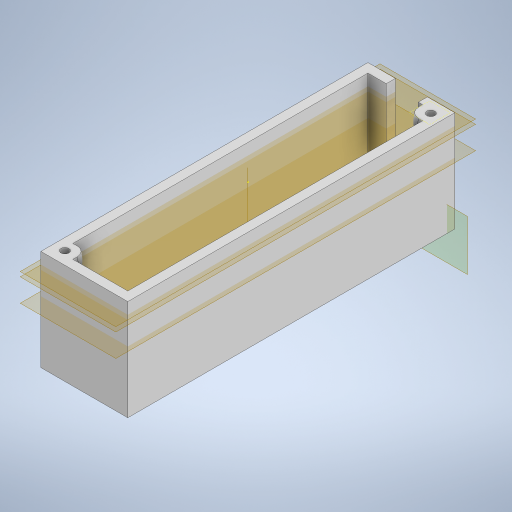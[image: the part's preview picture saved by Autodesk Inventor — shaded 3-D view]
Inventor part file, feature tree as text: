
AUTODESK INVENTOR PART (.ipt)
format: ipt  version: 2024 (Build 280153020, 153B)  size: 375,808 bytes
history: native  units: mm
features: sketch x9, extrude x6, plane x4, hole x1, loft x1, fillet x1, pattern_circular x1, projected_geometry x1, other x1
ambient origin geometry x8: Origin, YZ Plane, XZ Plane, XY Plane, X Axis, Y Axis, Z Axis, Center Point
bodies: Solid1 (feature_tree)
feature tree (25):
  sketch  "Sketch1"  dims[d0=30.0mm d1=135.0mm]
  extrude  "Extrusion1"  Depth=135.0mm
  extrude  "Extrusion2"  Depth=44.0mm TaperAngle=0.0deg
  hole  "Hole1"  [1 undecoded]
  plane  "Work Plane1"
  extrude  "Extrusion3"  Depth=14.0mm
  sketch  "Sketch4"  dims[d11=80.0mm]
  extrude  "Extrusion4"  Depth=10.25mm TaperAngle=0.0deg
  plane  "Work Plane2"
  sketch  "Sketch6"  dims[d20=50.0mm d21=10.25mm d22=0.0mm]
  plane  "Work Plane3"
  sketch  "Sketch7"  dims[d31=21.0mm d32=0.0mm d33=-7.0mm d34=-10.0mm]
  sketch  "Sketch8"  dims[d35=8.0mm d36=8.0mm]
  loft  "Loft1"
  fillet  "Fillet2"  [1 undecoded]
  plane  "Work Plane4"
  sketch  "Sketch9"  dims[d39=9.0mm d40=9.0mm d41=0.0mm d42=90.0deg d43=0.0mm d44=90.0deg d45=0.0mm d46=90.0deg d47=4.25mm d48=-5.0mm d49=5.0mm d50=2.8194mm d51=3.5mm d52=2.75mm d53=0.0mm d54=13.0mm d55=0.0mm d56=20.0mm d57=180.0deg]
  extrude  "Extrusion5"  Depth=8.0mm
  extrude  "Extrusion6"  Depth=2.75mm
  pattern_circular  "Circular Pattern1"  Angle=90.0deg  [1 undecoded]
  sketch  "Sketch2"  dims[d2=4.0mm d3=44.0mm d4=0.0mm]
  sketch  "Sketch3"  dims[d5=4.0mm d6=0.0mm d10=40.0mm]
  sketch  "Sketch5"  dims[d12=5.0mm d13=6.0mm d14=9.5mm d15=2.0mm d16=90.0deg d17=8.0mm d18=20.594885mm d19=14.0mm]
  projected_geometry  "Projected Loop1"
  other  "Work Axis1"
note: 3 required parameter values undecoded (feature->parameter linkage not recoverable at this tier; creation-order binding heuristic only, values carry confidence <= 0.55)
